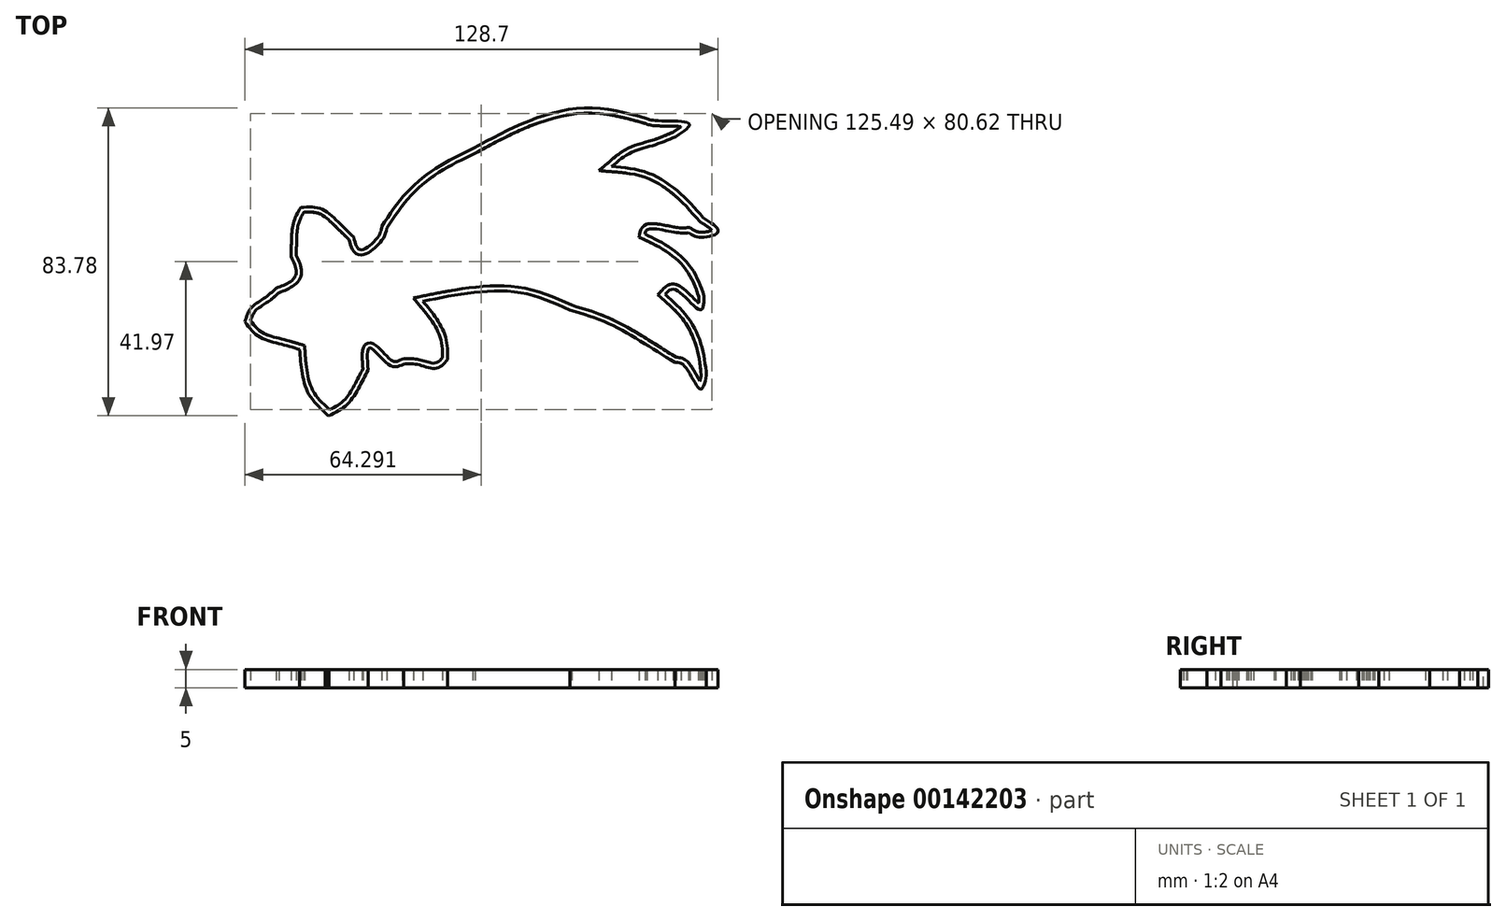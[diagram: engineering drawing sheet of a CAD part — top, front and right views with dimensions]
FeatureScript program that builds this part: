
annotation { "Feature Type Name" : "Feature", "Feature Type Description" : "" }
export const myFeature = defineFeature(function(context is Context, id is Id, definition is map)
    precondition{}
    {
        {
            var Q0;
            Q0=qCreatedBy(makeId("Top.planeOp"),FACE);
            var sketch = newSketch(context, id + "F0", { "sketchPlane" : qUnion([Q0])});
            skFitSpline(sketch, "E0", {"points": [v(-412.44, -400.46) * mm, v(-454.99, -353.52) * mm, v(-475.67, -290.73) * mm, v(-481.83, -228.57) * mm]});
            skFitSpline(sketch, "E1", {"points": [v(-481.83, -228.57) * mm, v(-535.33, -213.35) * mm, v(-591.58, -194.23) * mm, v(-630.87, -153.36) * mm]});
            skFitSpline(sketch, "E2", {"points": [v(-630.87, -153.36) * mm, v(-614.09, -115.43) * mm, v(-577.51, -88.42) * mm, v(-545.97, -61.75) * mm]});
            skFitSpline(sketch, "E3", {"points": [v(-545.97, -61.75) * mm, v(-506.88, -43.8) * mm, v(-491, -19.55) * mm, v(-505.5, 24.06) * mm]});
            skFitSpline(sketch, "E4", {"points": [v(-505.5, 24.06) * mm, v(-504.12, 69.47) * mm, v(-498.66, 116.73) * mm, v(-479.13, 157.9) * mm]});
            skFitSpline(sketch, "E5", {"points": [v(-479.13, 157.9) * mm, v(-423.02, 153.8) * mm, v(-374.22, 115.55) * mm, v(-334.7, 77.33) * mm]});
            skFitSpline(sketch, "E6", {"points": [v(-334.7, 77.33) * mm, v(-316.76, 42.67) * mm, v(-268.4, 78.66) * mm, v(-258.52, 106.37) * mm]});
            skFitSpline(sketch, "E7", {"points": [v(-258.52, 106.37) * mm, v(-194.17, 194.65) * mm, v(-108.02, 266.59) * mm, v(-11.08, 317.37) * mm]});
            skFitSpline(sketch, "E8", {"points": [v(-11.08, 317.37) * mm, v(133.76, 389.87) * mm, v(300.93, 428.73) * mm, v(462.78, 399.3) * mm]});
            skFitSpline(sketch, "E9", {"points": [v(462.78, 399.3) * mm, v(487.4, 393.9) * mm, v(577.22, 385.72) * mm, v(540.03, 350.08) * mm]});
            skFitSpline(sketch, "E10", {"points": [v(540.03, 350.08) * mm, v(480.5, 326.91) * mm, v(418.64, 306.87) * mm, v(366.54, 269.08) * mm]});
            skFitSpline(sketch, "E11", {"points": [v(366.54, 269.08) * mm, v(461.8, 252.93) * mm, v(548.94, 199.43) * mm, v(615.14, 130.1) * mm]});
            skFitSpline(sketch, "E12", {"points": [v(615.14, 130.1) * mm, v(655.76, 91.94) * mm, v(608.78, 76.51) * mm, v(575.19, 88.87) * mm]});
            skFitSpline(sketch, "E13", {"points": [v(575.19, 88.87) * mm, v(541.1, 89.61) * mm, v(465.75, 98.5) * mm, v(456.83, 85) * mm]});
            skFitSpline(sketch, "E14", {"points": [v(456.83, 85) * mm, v(525.9, 47.8) * mm, v(585.57, -11.3) * mm, v(617.78, -83.23) * mm]});
            skFitSpline(sketch, "E15", {"points": [v(617.78, -83.23) * mm, v(607.29, -120.85) * mm, v(539.68, -65.79) * mm, v(511.88, -78.87) * mm]});
            skFitSpline(sketch, "E16", {"points": [v(511.88, -78.87) * mm, v(570.88, -138) * mm, v(610.42, -217.01) * mm, v(624.34, -299.22) * mm]});
            skFitSpline(sketch, "E17", {"points": [v(624.34, -299.22) * mm, v(607.93, -336.34) * mm, v(563.9, -272.9) * mm, v(538.23, -264.22) * mm]});
            skFitSpline(sketch, "E18", {"points": [v(538.23, -264.22) * mm, v(448, -207.57) * mm, v(353.32, -155.72) * mm, v(252.99, -121.35) * mm]});
            skFitSpline(sketch, "E19", {"points": [v(252.99, -121.35) * mm, v(125.41, -75.22) * mm, v(-14.74, -74.24) * mm, v(-146.95, -97.62) * mm]});
            skFitSpline(sketch, "E20", {"points": [v(-146.95, -97.62) * mm, v(-111.14, -142.8) * mm, v(-84.45, -198.15) * mm, v(-79.7, -256.31) * mm]});
            skFitSpline(sketch, "E21", {"points": [v(-79.7, -256.31) * mm, v(-111.06, -279.51) * mm, v(-160.9, -269.65) * mm, v(-198.88, -268.33) * mm]});
            skFitSpline(sketch, "E22", {"points": [v(-198.88, -268.33) * mm, v(-236.5, -271.73) * mm, v(-291.1, -224.3) * mm, v(-295.67, -283.51) * mm]});
            skFitSpline(sketch, "E23", {"points": [v(-295.67, -283.51) * mm, v(-321.03, -332.8) * mm, v(-354.52, -379.47) * mm, v(-402.4, -409.11) * mm]});
            skLineSegment(sketch, "E24", {"start": v(-402.4, -409.11) * mm, "end": v(-405.78, -406.93) * mm});
            skLineSegment(sketch, "E25", {"start": v(-405.78, -406.93) * mm, "end": v(-412.44, -400.46) * mm});
            skLineSegment(sketch, "E26", {"start": v(-412.44, -400.46) * mm, "end": v(-412.44, -400.46) * mm});
            skLineSegment(sketch, "E27", {"start": v(-412.44, -400.46) * mm, "end": v(-402.4, -409.11) * mm});
            skSolve(sketch);
        }
        {
            var Q0;
            Q0 = qSketchRegion(id + "F0", true);
            extrude(context, id + "F1", {"entities" : qUnion([Q0]), "depth" : 64.87 * mm});
        }
        {
            var Q0;
            Q0=makeQuery(id+"F1.opExtrude","SWEPT_BODY",BODY,{"disambiguationData":[OSD([sQuery(id+"F0.wireOp",EDGE,"E0"),sQuery(id+"F0.wireOp",EDGE,"E1"),sQuery(id+"F0.wireOp",EDGE,"E2"),sQuery(id+"F0.wireOp",EDGE,"E3"),sQuery(id+"F0.wireOp",EDGE,"E4"),sQuery(id+"F0.wireOp",EDGE,"E5"),sQuery(id+"F0.wireOp",EDGE,"E6"),sQuery(id+"F0.wireOp",EDGE,"E7"),sQuery(id+"F0.wireOp",EDGE,"E8"),sQuery(id+"F0.wireOp",EDGE,"E9"),sQuery(id+"F0.wireOp",EDGE,"E10"),sQuery(id+"F0.wireOp",EDGE,"E11"),sQuery(id+"F0.wireOp",EDGE,"E12"),sQuery(id+"F0.wireOp",EDGE,"E13"),sQuery(id+"F0.wireOp",EDGE,"E14"),sQuery(id+"F0.wireOp",EDGE,"E15"),sQuery(id+"F0.wireOp",EDGE,"E16"),sQuery(id+"F0.wireOp",EDGE,"E17"),sQuery(id+"F0.wireOp",EDGE,"E18"),sQuery(id+"F0.wireOp",EDGE,"E19"),sQuery(id+"F0.wireOp",EDGE,"E20"),sQuery(id+"F0.wireOp",EDGE,"E21"),sQuery(id+"F0.wireOp",EDGE,"E22"),sQuery(id+"F0.wireOp",EDGE,"E23"),sQuery(id+"F0.wireOp",EDGE,"E24"),sQuery(id+"F0.wireOp",EDGE,"E25"),sQuery(id+"F0.wireOp",EDGE,"E27")])]});
            var Q1;
            Q1=qCreatedBy(makeId("Origin.pointOp"),VERTEX);
            transform(context, id + "F2", {"entities" : qUnion([Q0]), "transformType" : TransformType.SCALE_UNIFORMLY, "scale" : 0.1, "scalePoint" : qUnion([Q1]), "makeCopy" : false});
        }
        {
            var Q0;
            Q0=qCreatedBy(makeId("Top.planeOp"),FACE);
            cPlane(context, id + "F3", {"entities" : qUnion([Q0]), "cplaneType" : CPlaneType.OFFSET, "offset" : 5 * mm, "width" : 150 * mm, "height" : 150 * mm});
        }
        {
            var Q0;
            Q0=makeQuery(id+"F1.opExtrude","CAP_FACE",FACE,{"disambiguationData":[OSD([sQuery(id+"F0.wireOp",EDGE,"E0"),sQuery(id+"F0.wireOp",EDGE,"E1"),sQuery(id+"F0.wireOp",EDGE,"E2"),sQuery(id+"F0.wireOp",EDGE,"E3"),sQuery(id+"F0.wireOp",EDGE,"E4"),sQuery(id+"F0.wireOp",EDGE,"E5"),sQuery(id+"F0.wireOp",EDGE,"E6"),sQuery(id+"F0.wireOp",EDGE,"E7"),sQuery(id+"F0.wireOp",EDGE,"E8"),sQuery(id+"F0.wireOp",EDGE,"E9"),sQuery(id+"F0.wireOp",EDGE,"E10"),sQuery(id+"F0.wireOp",EDGE,"E11"),sQuery(id+"F0.wireOp",EDGE,"E12"),sQuery(id+"F0.wireOp",EDGE,"E13"),sQuery(id+"F0.wireOp",EDGE,"E14"),sQuery(id+"F0.wireOp",EDGE,"E15"),sQuery(id+"F0.wireOp",EDGE,"E16"),sQuery(id+"F0.wireOp",EDGE,"E17"),sQuery(id+"F0.wireOp",EDGE,"E18"),sQuery(id+"F0.wireOp",EDGE,"E19"),sQuery(id+"F0.wireOp",EDGE,"E20"),sQuery(id+"F0.wireOp",EDGE,"E21"),sQuery(id+"F0.wireOp",EDGE,"E22"),sQuery(id+"F0.wireOp",EDGE,"E23"),sQuery(id+"F0.wireOp",EDGE,"E24"),sQuery(id+"F0.wireOp",EDGE,"E25"),sQuery(id+"F0.wireOp",EDGE,"E27")])],"isStart":false});
            var Q1;
            Q1=qCreatedBy(id+"F3.planeOp",FACE);
            extrude(context, id + "F4", {"entities" : qUnion([Q0]), "operationType" : NewBodyOperationType.REMOVE, "endBound" : BoundingType.UP_TO_SURFACE, "oppositeDirection" : true, "endBoundEntityFace" : qUnion([Q1]), "depth" : 25 * mm});
        }
        {
            var Q0;
            Q0=makeQuery(id+"F4.boolean.opBoolean","COPY",FACE,{"derivedFrom":makeQuery(id+"F4.opExtrude","CAP_FACE",FACE,{"disambiguationData":[OSD([sQuery(id+"F0.wireOp",EDGE,"E0"),sQuery(id+"F0.wireOp",EDGE,"E1"),sQuery(id+"F0.wireOp",EDGE,"E2"),sQuery(id+"F0.wireOp",EDGE,"E3"),sQuery(id+"F0.wireOp",EDGE,"E4"),sQuery(id+"F0.wireOp",EDGE,"E5"),sQuery(id+"F0.wireOp",EDGE,"E6"),sQuery(id+"F0.wireOp",EDGE,"E7"),sQuery(id+"F0.wireOp",EDGE,"E8"),sQuery(id+"F0.wireOp",EDGE,"E9"),sQuery(id+"F0.wireOp",EDGE,"E10"),sQuery(id+"F0.wireOp",EDGE,"E11"),sQuery(id+"F0.wireOp",EDGE,"E12"),sQuery(id+"F0.wireOp",EDGE,"E13"),sQuery(id+"F0.wireOp",EDGE,"E14"),sQuery(id+"F0.wireOp",EDGE,"E15"),sQuery(id+"F0.wireOp",EDGE,"E16"),sQuery(id+"F0.wireOp",EDGE,"E17"),sQuery(id+"F0.wireOp",EDGE,"E18"),sQuery(id+"F0.wireOp",EDGE,"E19"),sQuery(id+"F0.wireOp",EDGE,"E20"),sQuery(id+"F0.wireOp",EDGE,"E21"),sQuery(id+"F0.wireOp",EDGE,"E22"),sQuery(id+"F0.wireOp",EDGE,"E23"),sQuery(id+"F0.wireOp",EDGE,"E24"),sQuery(id+"F0.wireOp",EDGE,"E25"),sQuery(id+"F0.wireOp",EDGE,"E27")])],"isStart":false})});
            var Q1;
            Q1=makeQuery(id+"F1.opExtrude","CAP_FACE",FACE,{"disambiguationData":[OSD([sQuery(id+"F0.wireOp",EDGE,"E0"),sQuery(id+"F0.wireOp",EDGE,"E1"),sQuery(id+"F0.wireOp",EDGE,"E2"),sQuery(id+"F0.wireOp",EDGE,"E3"),sQuery(id+"F0.wireOp",EDGE,"E4"),sQuery(id+"F0.wireOp",EDGE,"E5"),sQuery(id+"F0.wireOp",EDGE,"E6"),sQuery(id+"F0.wireOp",EDGE,"E7"),sQuery(id+"F0.wireOp",EDGE,"E8"),sQuery(id+"F0.wireOp",EDGE,"E9"),sQuery(id+"F0.wireOp",EDGE,"E10"),sQuery(id+"F0.wireOp",EDGE,"E11"),sQuery(id+"F0.wireOp",EDGE,"E12"),sQuery(id+"F0.wireOp",EDGE,"E13"),sQuery(id+"F0.wireOp",EDGE,"E14"),sQuery(id+"F0.wireOp",EDGE,"E15"),sQuery(id+"F0.wireOp",EDGE,"E16"),sQuery(id+"F0.wireOp",EDGE,"E17"),sQuery(id+"F0.wireOp",EDGE,"E18"),sQuery(id+"F0.wireOp",EDGE,"E19"),sQuery(id+"F0.wireOp",EDGE,"E20"),sQuery(id+"F0.wireOp",EDGE,"E21"),sQuery(id+"F0.wireOp",EDGE,"E22"),sQuery(id+"F0.wireOp",EDGE,"E23"),sQuery(id+"F0.wireOp",EDGE,"E24"),sQuery(id+"F0.wireOp",EDGE,"E25"),sQuery(id+"F0.wireOp",EDGE,"E27")])],"isStart":true});
            shell(context, id + "F5", {"entities" : qUnion([Q0, Q1]), "thickness" : 1.4 * mm});
        }
    });
